# Revit family: Faucet-Kitchen-KOHLER-ALEO-K-99176T
name_source: partatom
category: Plumbing Fixtures
units: mm (PartAtom-declared; Revit-internal decimal feet)

## family parameters
Cut with Voids When Loaded = No
Host = Face
OmniClass Number = 23.31.11.00
OmniClass Title = Faucets
Part Type = Normal
Room Calculation Point = No
Round Connector Dimension = Use Diameter
Shared = No

## types (5) — shared parameters
ADA Compliant = No
Assembly Code = D2010
CW Connection = Yes
Cold Water Inlet = Cold Water Inlet
Date Modified = 07/06/2023
Default Elevation = 36"
Drain Included = No
Faucet Hole Spacing = 0"
Flow Rate = 2 GPM
HW Connection = Yes
Handle Clearance = 3 5/8"
Height = 11 3/16"
Hot Water Inlet = Hot Water Inlet
Length = 8 11/16"
Manufacturer = Kohler Co.
Master Format 2014 = 22 41 39
Master Format 2014 Name = Residential Faucets, Supplies, and Trim
Material = Premiun Metal Construction
Pressure = 60.00 psi
Product Name = Aleo
Spout Reach = 8 11/16"
URL = http://www.kohler.com.cn
Vent Connection = No
Waste Connection = No
Waste Water Outlet = Waste Water Outlet
WaterSense Certified = No
Width = 1 13/16"

## per-type parameters (varying)
| type | Description | Finish | Model | Type |
| 1.75 GPM, 2MB-Vibrant Brushed Moderne Brass | Tube Spout Faucet | Kohler-Metal-2MB-Vibrant_Brushed_Moderne_Brass | K-99176T-4E-2MB | 1 |
| 1.75 GPM, BL-Matte_Black | Tube Spout Faucet | Kohler-Metal-BL-Matte_Black | K-99176T-4E-BL | 2 |
| 1.75 GPM, CP-Polished Chrome | Tube Spout Faucet | Kohler-Metal-CP-Polished_Chrome | K-99176T-4E-CP | 3 |
| 1.75 GPM, VS-Vibrant Stainless | Tube Spout Faucet | Kohler-Metal-VS-Vibrant_Stainless | K-99176T-4E-VS | 4 |
| 2.2 GPM, CP-Polished Chrome | Single kitchen tap | Kohler-Metal-CP-Polished_Chrome | K-99176T-4-CP | 5 |

## geometry (parser evidence)
native form markers: Sweep x5
no freeform markers — native parametric forms only
